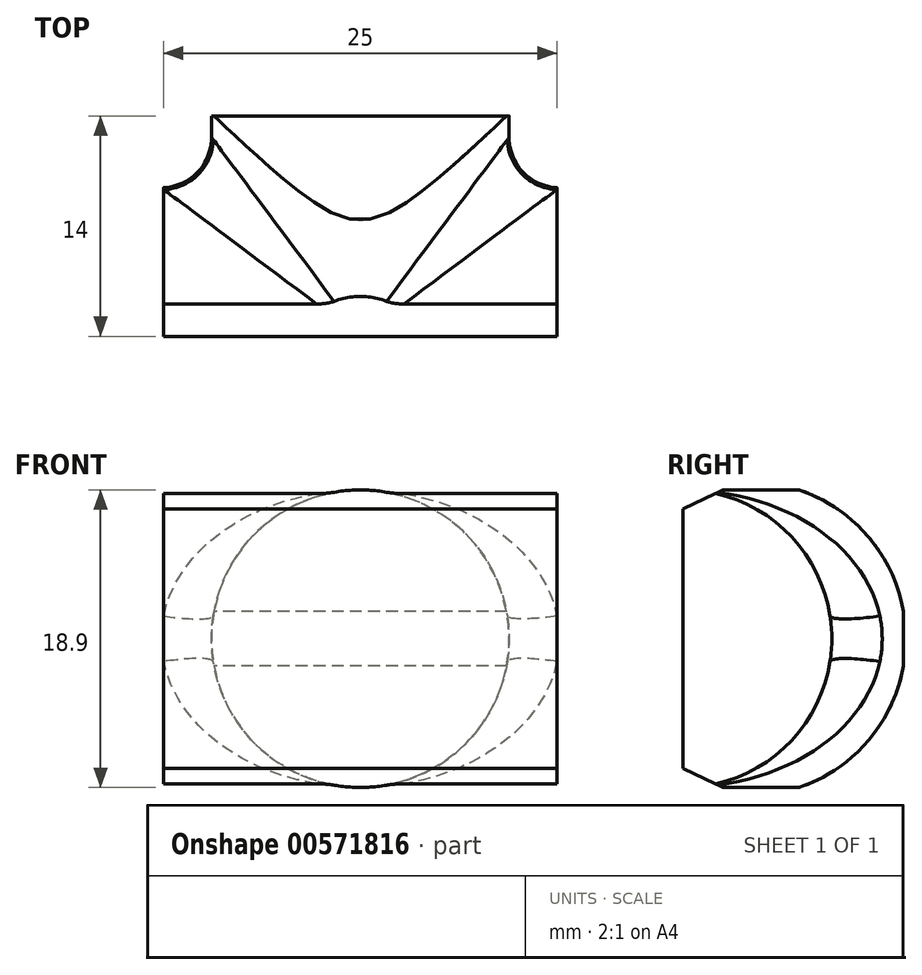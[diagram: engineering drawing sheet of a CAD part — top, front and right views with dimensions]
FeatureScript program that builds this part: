
annotation { "Feature Type Name" : "Feature", "Feature Type Description" : "" }
export const myFeature = defineFeature(function(context is Context, id is Id, definition is map)
    precondition{}
    {
        {
            var Q0;
            Q0=qCreatedBy(makeId("Front.planeOp"),FACE);
            var sketch = newSketch(context, id + "F0", { "sketchPlane" : qUnion([Q0])});
            skCircle(sketch, "E0", {"center": v(0, 0) * mm, "radius": 9.45 * mm});
            skSolve(sketch);
        }
        {
            var Q0;
            Q0 = qSketchRegion(id + "F0", true);
            extrude(context, id + "F1", {"entities" : qUnion([Q0]), "oppositeDirection" : true, "depth" : 14 * mm, "offsetDistance" : 25 * mm});
        }
        {
            var Q0;
            Q0=qCreatedBy(makeId("Right.planeOp"),FACE);
            var sketch = newSketch(context, id + "F2", { "sketchPlane" : qUnion([Q0])});
            skCircle(sketch, "E1", {"center": v(0, 0) * mm, "radius": 9.45 * mm});
            skSolve(sketch);
        }
        {
            var Q0;
            Q0 = qSketchRegion(id + "F2", true);
            extrude(context, id + "F3", {"entities" : qUnion([Q0]), "operationType" : NewBodyOperationType.ADD, "endBound" : BoundingType.SYMMETRIC, "depth" : 25 * mm, "offsetDistance" : 25 * mm});
        }
        {
            var Q0;
            Q0=makeQuery(id+"F3.boolean.opBoolean","INTERSECT",EDGE,{"disambiguationData":[OD(1.0)],"derivedFrom":[makeQuery(id+"F1.opExtrude","SWEPT_FACE",FACE,{"disambiguationData":[OSD([sQuery(id+"F0.wireOp",EDGE,"E0")])]}),makeQuery(id+"F3.opExtrude","SWEPT_FACE",FACE,{"disambiguationData":[OSD([sQuery(id+"F2.wireOp",EDGE,"E1")])]})]});
            fillet(context, id + "F4", {"entities" : qUnion([Q0]), "radius" : 3.2 * mm, "tangentPropagation" : true, "allowEdgeOverflow" : false});
        }
        {
            var Q0;
            Q0=makeQuery(id+"F3.boolean.opBoolean","INTERSECT",EDGE,{"disambiguationData":[OD(0.0)],"derivedFrom":[makeQuery(id+"F1.opExtrude","SWEPT_FACE",FACE,{"disambiguationData":[OSD([sQuery(id+"F0.wireOp",EDGE,"E0")])]}),makeQuery(id+"F3.opExtrude","SWEPT_FACE",FACE,{"disambiguationData":[OSD([sQuery(id+"F2.wireOp",EDGE,"E1")])]})]});
            fillet(context, id + "F5", {"entities" : qUnion([Q0]), "radius" : 3.2 * mm, "tangentPropagation" : true, "allowEdgeOverflow" : false});
        }
        {
            var Q0;
            Q0=makeQuery(id+"F1.opExtrude","CAP_FACE",FACE,{"disambiguationData":[OSD([sQuery(id+"F0.wireOp",EDGE,"E0")])],"isStart":false});
            var sketch = newSketch(context, id + "F6", { "sketchPlane" : qUnion([Q0])});
            skCircle(sketch, "E2", {"center": v(0, 0) * mm, "radius": 5 * mm});
            skSolve(sketch);
        }
        {
            var Q0;
            Q0=makeQuery(id+"F3.opExtrude","CAP_FACE",FACE,{"disambiguationData":[OSD([sQuery(id+"F2.wireOp",EDGE,"E1")])],"isStart":true});
            var sketch = newSketch(context, id + "F7", { "sketchPlane" : qUnion([Q0])});
            skLineSegment(sketch, "E3.bottom", {"start": v(0, 11.55) * mm, "end": v(12, 11.55) * mm});
            skLineSegment(sketch, "E3.top", {"start": v(0, -11.8) * mm, "end": v(12, -11.8) * mm});
            skLineSegment(sketch, "E3.left", {"start": v(0, 11.55) * mm, "end": v(0, -11.8) * mm});
            skLineSegment(sketch, "E3.right", {"start": v(12, 11.55) * mm, "end": v(12, -11.8) * mm});
            skSolve(sketch);
        }
        {
            var Q0;
            {var subQ0=sQuery(id+"F7.wireOp",EDGE,"E3.left");var subQ1=makeQuery(id+"F3.opExtrude","CAP_EDGE",EDGE,{"disambiguationData":[OSD([sQuery(id+"F2.wireOp",EDGE,"E1")])],"isStart":true});var subQ2=makeQuery(id+"F7.imprint","INTERSECT",VERTEX,{"disambiguationData":[OD(0.0)],"derivedFrom":[subQ1,subQ0]});Q0=makeQuery(id+"F7.imprint","IMPRINT",FACE,{"disambiguationData":[TD([[makeQuery(id+"F7.imprint","IMPRINT",EDGE,{"disambiguationData":[TD([[subQ2,-1.0]])],"derivedFrom":subQ0}),1.0]])]});}
            extrude(context, id + "F8", {"entities" : qUnion([Q0]), "operationType" : NewBodyOperationType.REMOVE, "oppositeDirection" : true, "depth" : 39.7 * mm, "offsetDistance" : 25 * mm});
        }
        {
            var Q0;
            Q0=makeQuery(id+"F3.opExtrude","CAP_FACE",FACE,{"disambiguationData":[OSD([sQuery(id+"F2.wireOp",EDGE,"E1")])],"isStart":true});
            var sketch = newSketch(context, id + "F9", { "sketchPlane" : qUnion([Q0])});
            skLineSegment(sketch, "E4", {"start": v(-11.17, 0) * mm, "end": v(0, 0) * mm});
            skPoint(sketch, "E5", {"position": v(-4.15, 0) * mm});
            skLineSegment(sketch, "E6", {"start": v(-3.57, 9.93) * mm, "end": v(2.53, 7.04) * mm});
            skLineSegment(sketch, "E7", {"start": v(2.53, 7.04) * mm, "end": v(1.38, 10.57) * mm});
            skLineSegment(sketch, "E8", {"start": v(1.38, 10.57) * mm, "end": v(-3.57, 9.93) * mm});
            skLineSegment(sketch, "E9.MirrorCS", {"start": v(1.38, -10.57) * mm, "end": v(-3.57, -9.93) * mm});
            skLineSegment(sketch, "E10.MirrorCS", {"start": v(2.53, -7.04) * mm, "end": v(1.38, -10.57) * mm});
            skLineSegment(sketch, "E11.MirrorCS", {"start": v(-3.57, -9.93) * mm, "end": v(2.53, -7.04) * mm});
            skSolve(sketch);
        }
        {
            var Q0;
            Q0 = qSketchRegion(id + "F9", true);
            extrude(context, id + "F10", {"entities" : qUnion([Q0]), "operationType" : NewBodyOperationType.REMOVE, "oppositeDirection" : true, "depth" : 25 * mm, "offsetDistance" : 25 * mm});
        }
        {
            var Q0;
            Q0=makeQuery(id+"F3.opExtrude","CAP_FACE",FACE,{"disambiguationData":[OSD([sQuery(id+"F2.wireOp",EDGE,"E1")])],"isStart":true});
            var sketch = newSketch(context, id + "F11", { "sketchPlane" : qUnion([Q0])});
            skCircle(sketch, "E12", {"center": v(-4.17, 0) * mm, "radius": 9.98 * mm});
            skCircle(sketch, "E13", {"center": v(-4.17, 0) * mm, "radius": 15 * mm});
            skSolve(sketch);
        }
        {
            var Q0;
            Q0 = qSketchRegion(id + "F11", true);
            extrude(context, id + "F12", {"entities" : qUnion([Q0]), "operationType" : NewBodyOperationType.REMOVE, "oppositeDirection" : true, "depth" : 25 * mm, "offsetDistance" : 25 * mm});
        }
        {
            var Q0;
            Q0=sQuery(id+"F6.wireOp",EDGE,"E2");
            extrude(context, id + "F13", {"bodyType" : ToolBodyType.SURFACE, "surfaceEntities" : qUnion([Q0]), "depth" : 57.3 * mm, "offsetDistance" : 25 * mm});
        }
        {
            var Q0;
            Q0=sQuery(id+"F6.wireOp",EDGE,"E2");
            extrude(context, id + "F14", {"bodyType" : ToolBodyType.SURFACE, "surfaceOperationType" : NewSurfaceOperationType.ADD, "surfaceEntities" : qUnion([Q0]), "depth" : 69.7 * mm, "offsetDistance" : 25 * mm});
        }
    });
